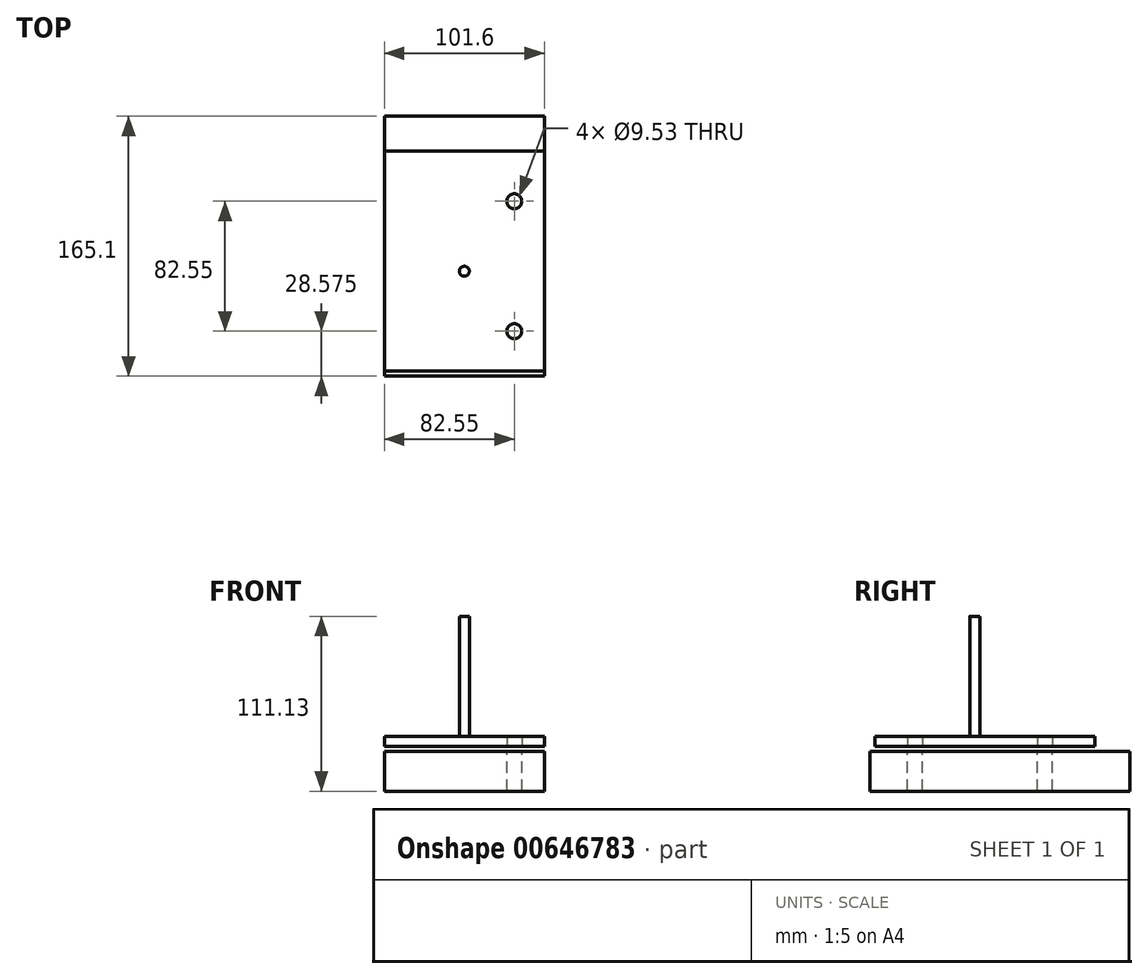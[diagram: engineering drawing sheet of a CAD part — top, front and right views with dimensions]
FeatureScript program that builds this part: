
annotation { "Feature Type Name" : "Feature", "Feature Type Description" : "" }
export const myFeature = defineFeature(function(context is Context, id is Id, definition is map)
    precondition{}
    {
        {
            var Q0;
            Q0=qCreatedBy(makeId("Top.planeOp"),FACE);
            cPlane(context, id + "F0", {"entities" : qUnion([Q0]), "cplaneType" : CPlaneType.OFFSET, "offset" : 3.17 * mm, "width" : 152.4 * mm, "height" : 152.4 * mm});
        }
        {
            var Q0;
            Q0=qCreatedBy(makeId("Top.planeOp"),FACE);
            var sketch = newSketch(context, id + "F1", { "sketchPlane" : qUnion([Q0])});
            skLineSegment(sketch, "E0.bottom", {"start": v(0, 0) * mm, "end": v(-101.6, 0) * mm});
            skLineSegment(sketch, "E0.top", {"start": v(0, 165.1) * mm, "end": v(-101.6, 165.1) * mm});
            skLineSegment(sketch, "E0.left", {"start": v(0, 0) * mm, "end": v(0, 165.1) * mm});
            skLineSegment(sketch, "E0.right", {"start": v(-101.6, 0) * mm, "end": v(-101.6, 165.1) * mm});
            skCircle(sketch, "E1", {"center": v(-19.05, 28.58) * mm, "radius": 4.76 * mm});
            skCircle(sketch, "E2", {"center": v(-19.05, 111.13) * mm, "radius": 4.76 * mm});
            skSolve(sketch);
        }
        {
            var Q0;
            Q0=makeQuery(id+"F1.imprint","IMPRINT",FACE,{"disambiguationData":[TD([[makeQuery(id+"F1.imprint","IMPRINT",EDGE,{"derivedFrom":sQuery(id+"F1.wireOp",EDGE,"E0.bottom")}),-1.0]])]});
            extrude(context, id + "F2", {"entities" : qUnion([Q0]), "oppositeDirection" : true, "depth" : 25.4 * mm, "offsetDistance" : 25.4 * mm});
        }
        {
            var Q0;
            Q0=qCreatedBy(id+"F0.planeOp",FACE);
            var sketch = newSketch(context, id + "F3", { "sketchPlane" : qUnion([Q0])});
            skLineSegment(sketch, "E3.bottom", {"start": v(0, 3.18) * mm, "end": v(-101.6, 3.17) * mm});
            skLineSegment(sketch, "E3.top", {"start": v(0, 142.88) * mm, "end": v(-101.6, 142.88) * mm});
            skLineSegment(sketch, "E3.left", {"start": v(0, 3.17) * mm, "end": v(0, 142.88) * mm});
            skLineSegment(sketch, "E3.right", {"start": v(-101.6, 3.17) * mm, "end": v(-101.6, 142.88) * mm});
            skCircle(sketch, "E4", {"center": v(-19.05, 111.13) * mm, "radius": 4.76 * mm});
            skCircle(sketch, "E5", {"center": v(-19.05, 28.58) * mm, "radius": 4.76 * mm});
            skSolve(sketch);
        }
        {
            var Q0;
            Q0 = qSketchRegion(id + "F3", true);
            extrude(context, id + "F4", {"entities" : qUnion([Q0]), "operationType" : NewBodyOperationType.ADD, "depth" : 6.35 * mm, "offsetDistance" : 25.4 * mm});
        }
        {
            var Q0;
            Q0=makeQuery(id+"F4.opExtrude","CAP_FACE",FACE,{"disambiguationData":[OSD([sQuery(id+"F3.wireOp",EDGE,"E3.bottom"),sQuery(id+"F3.wireOp",EDGE,"E3.top"),sQuery(id+"F3.wireOp",EDGE,"E3.left"),sQuery(id+"F3.wireOp",EDGE,"E3.right"),sQuery(id+"F3.wireOp",EDGE,"E4"),sQuery(id+"F3.wireOp",EDGE,"E5")])],"isStart":false});
            var sketch = newSketch(context, id + "F5", { "sketchPlane" : qUnion([Q0])});
            skCircle(sketch, "E6", {"center": v(-50.8, 66.67) * mm, "radius": 3.18 * mm});
            skPoint(sketch, "E6.centerSnap0", {"position": v(-50.8, 3.17) * mm});
            skSolve(sketch);
        }
        {
            var Q0;
            Q0 = qSketchRegion(id + "F5", true);
            extrude(context, id + "F6", {"entities" : qUnion([Q0]), "operationType" : NewBodyOperationType.ADD, "depth" : 76.2 * mm, "offsetDistance" : 25.4 * mm});
        }
    });
